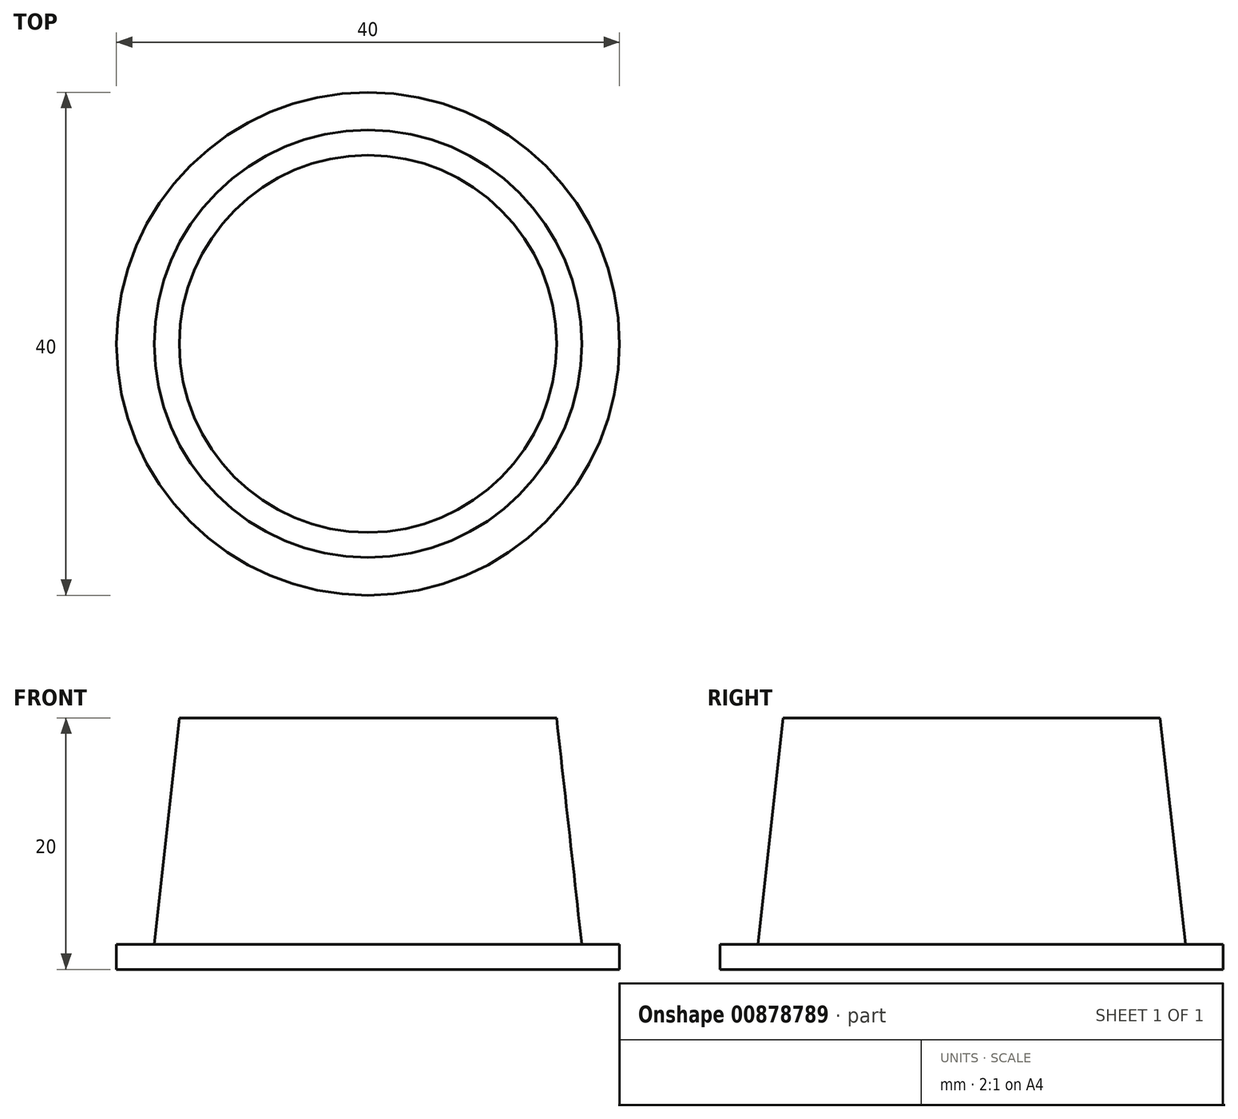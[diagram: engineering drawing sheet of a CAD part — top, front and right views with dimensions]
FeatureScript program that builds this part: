
annotation { "Feature Type Name" : "Feature", "Feature Type Description" : "" }
export const myFeature = defineFeature(function(context is Context, id is Id, definition is map)
    precondition{}
    {
        {
            var Q0;
            Q0=qCreatedBy(makeId("Front.planeOp"),FACE);
            var sketch = newSketch(context, id + "F0", { "sketchPlane" : qUnion([Q0])});
            skLineSegment(sketch, "E0", {"start": v(0, 0) * mm, "end": v(20, 0) * mm});
            skLineSegment(sketch, "E1", {"start": v(20, 0) * mm, "end": v(20, 2) * mm});
            skLineSegment(sketch, "E2", {"start": v(20, 2) * mm, "end": v(17, 2) * mm});
            skLineSegment(sketch, "E3", {"start": v(17, 2) * mm, "end": v(15, 20) * mm});
            skLineSegment(sketch, "E4", {"start": v(15, 20) * mm, "end": v(0, 20) * mm});
            skLineSegment(sketch, "E5", {"start": v(0, 20) * mm, "end": v(0, 0) * mm});
            skSolve(sketch);
        }
        {
            var Q0;
            Q0 = qSketchRegion(id + "F0", true);
            var Q1;
            Q1=sQuery(id+"F0.wireOp",EDGE,"E5");
            revolve(context, id + "F1", {"surfaceOperationType" : NewSurfaceOperationType.NEW, "entities" : qUnion([Q0]), "axis" : qUnion([Q1]), "revolveType" : RevolveType.FULL});
        }
    });
